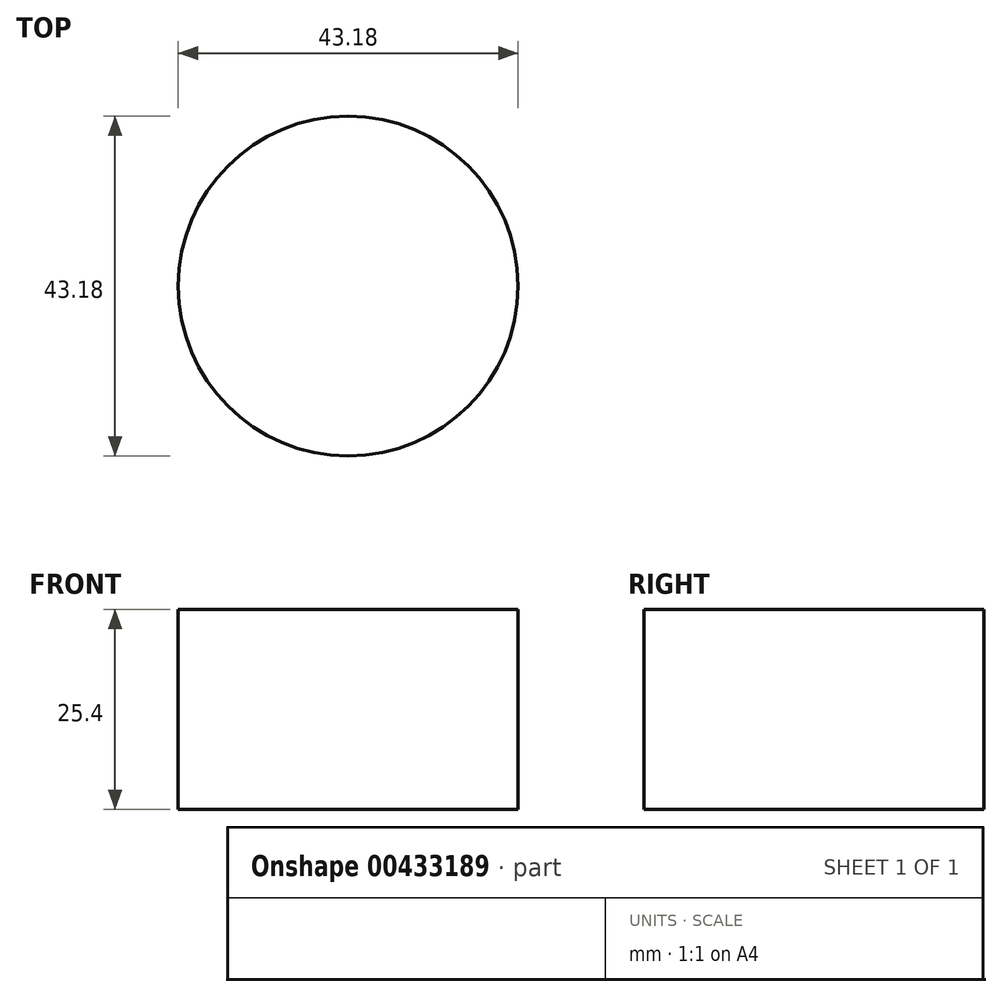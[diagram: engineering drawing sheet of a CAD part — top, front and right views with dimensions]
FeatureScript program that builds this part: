
annotation { "Feature Type Name" : "Feature", "Feature Type Description" : "" }
export const myFeature = defineFeature(function(context is Context, id is Id, definition is map)
    precondition{}
    {
        {
            var Q0;
            Q0=qCreatedBy(makeId("Top.planeOp"),FACE);
            var sketch = newSketch(context, id + "F0", { "sketchPlane" : qUnion([Q0])});
            skCircle(sketch, "E0", {"center": v(0, 0) * mm, "radius": 21.59 * mm});
            skSolve(sketch);
        }
        {
            var Q0;
            Q0=makeQuery(id+"F0.imprint","IMPRINT",FACE,{"disambiguationData":[TD([[makeQuery(id+"F0.imprint","IMPRINT",EDGE,{"derivedFrom":sQuery(id+"F0.wireOp",EDGE,"E0")}),1.0]])]});
            extrude(context, id + "F1", {"entities" : qUnion([Q0]), "depth" : 25.4 * mm});
        }
    });
